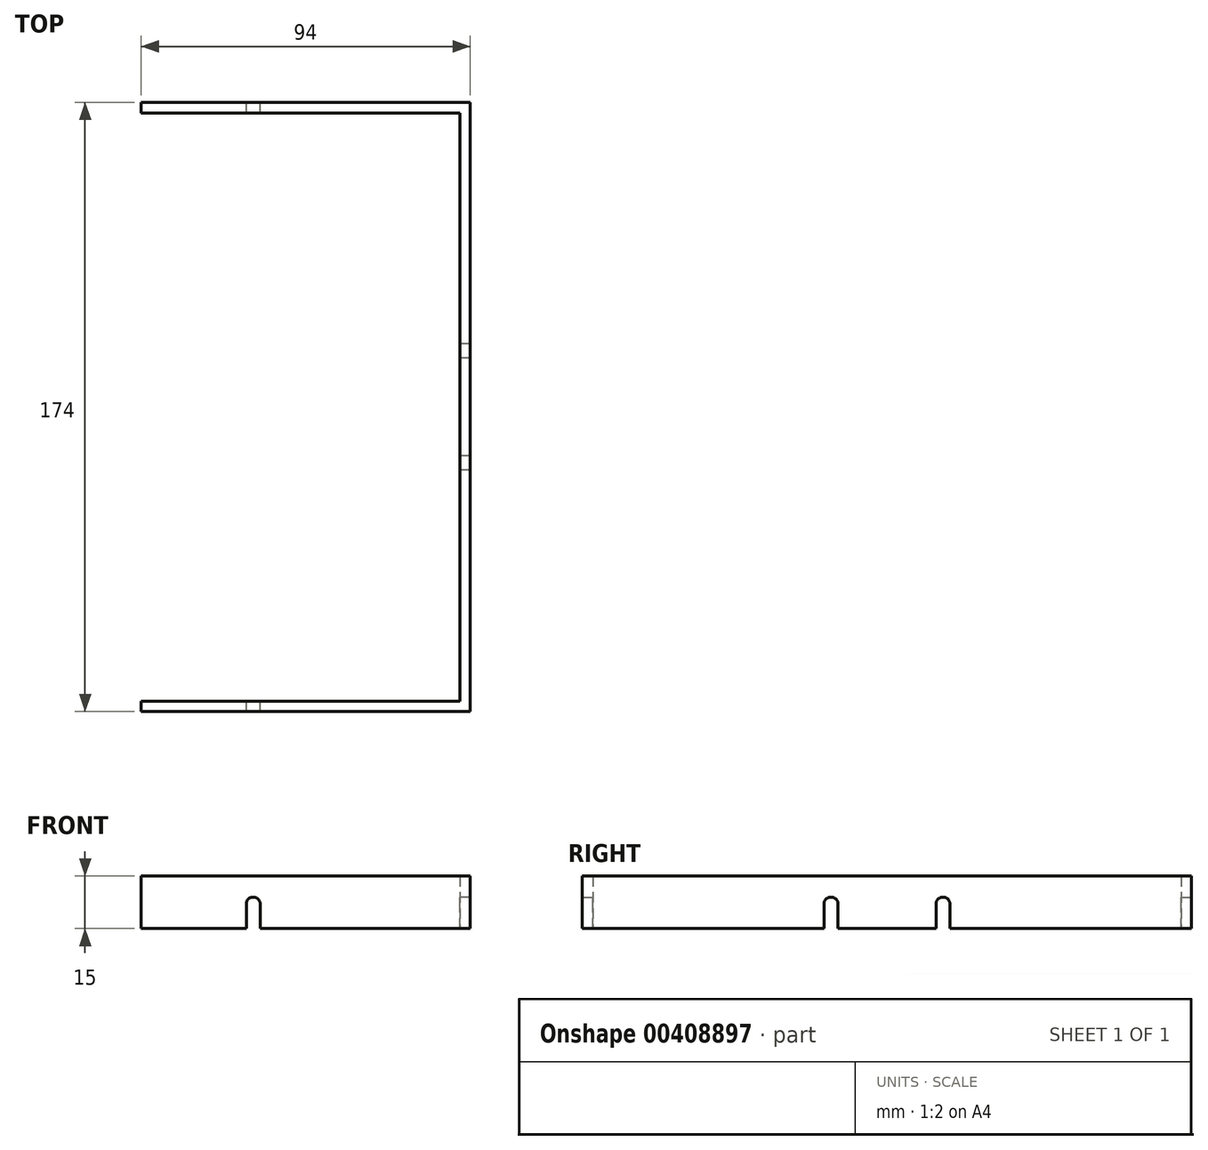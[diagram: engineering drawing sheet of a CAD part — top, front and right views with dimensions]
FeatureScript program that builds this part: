
annotation { "Feature Type Name" : "Feature", "Feature Type Description" : "" }
export const myFeature = defineFeature(function(context is Context, id is Id, definition is map)
    precondition{}
    {
        {
            var Q0;
            Q0=qCreatedBy(makeId("Top.planeOp"),FACE);
            var sketch = newSketch(context, id + "F0", { "sketchPlane" : qUnion([Q0])});
            skLineSegment(sketch, "E0.bottom", {"start": v(47, 87) * mm, "end": v(-47, 87) * mm});
            skLineSegment(sketch, "E0.top", {"start": v(47, -87) * mm, "end": v(-47, -87) * mm});
            skLineSegment(sketch, "E0.left", {"start": v(47, 87) * mm, "end": v(47, -87) * mm});
            skLineSegment(sketch, "E0.right", {"start": v(-47, 87) * mm, "end": v(-47, -87) * mm});
            skPoint(sketch, "E0.middle", {"position": v(0, 0) * mm});
            skSolve(sketch);
        }
        {
            var Q0;
            Q0=makeQuery(id+"F0.imprint","IMPRINT",FACE,{"disambiguationData":[TD([[makeQuery(id+"F0.imprint","IMPRINT",EDGE,{"derivedFrom":sQuery(id+"F0.wireOp",EDGE,"E0.bottom")}),1.0]])]});
            extrude(context, id + "F1", {"entities" : qUnion([Q0]), "depth" : 15 * mm});
        }
        {
            var Q0;
            Q0=makeQuery(id+"F1.opExtrude","CAP_FACE",FACE,{"disambiguationData":[OSD([sQuery(id+"F0.wireOp",EDGE,"E0.bottom"),sQuery(id+"F0.wireOp",EDGE,"E0.top"),sQuery(id+"F0.wireOp",EDGE,"E0.left"),sQuery(id+"F0.wireOp",EDGE,"E0.right")])],"isStart":false});
            var Q1;
            Q1=makeQuery(id+"F1.opExtrude","SWEPT_FACE",FACE,{"disambiguationData":[OSD([sQuery(id+"F0.wireOp",EDGE,"E0.right")])]});
            var Q2;
            Q2=makeQuery(id+"F1.opExtrude","CAP_FACE",FACE,{"disambiguationData":[OSD([sQuery(id+"F0.wireOp",EDGE,"E0.bottom"),sQuery(id+"F0.wireOp",EDGE,"E0.top"),sQuery(id+"F0.wireOp",EDGE,"E0.left"),sQuery(id+"F0.wireOp",EDGE,"E0.right")])],"isStart":true});
            shell(context, id + "F2", {"entities" : qUnion([Q0, Q1, Q2]), "thickness" : 3 * mm});
        }
        {
            var Q0;
            Q0=qCreatedBy(makeId("Right.planeOp"),FACE);
            var sketch = newSketch(context, id + "F3", { "sketchPlane" : qUnion([Q0])});
            skCircle(sketch, "E1", {"center": v(-16, 7) * mm, "radius": 2 * mm});
            skCircle(sketch, "E2.1.0.0", {"center": v(16, 7) * mm, "radius": 2 * mm});
            skLineSegment(sketch, "E2.direction1", {"start": v(-16, 7) * mm, "end": v(16, 7) * mm, "construction": true});
            skLineSegment(sketch, "E3.bottom", {"start": v(-18, 7) * mm, "end": v(-14, 7) * mm});
            skLineSegment(sketch, "E3.top", {"start": v(-18, 0) * mm, "end": v(-14, 0) * mm});
            skLineSegment(sketch, "E3.left", {"start": v(-18, 7) * mm, "end": v(-18, 0) * mm});
            skLineSegment(sketch, "E3.right", {"start": v(-14, 7) * mm, "end": v(-14, 0) * mm});
            skLineSegment(sketch, "E4.direction1", {"start": v(-14, 0) * mm, "end": v(18, 0) * mm, "construction": true});
            skLineSegment(sketch, "E5.1.0.0", {"start": v(18, 7) * mm, "end": v(18, 0) * mm});
            skLineSegment(sketch, "E5.1.0.1", {"start": v(14, 7) * mm, "end": v(18, 7) * mm});
            skLineSegment(sketch, "E5.1.0.2", {"start": v(14, 7) * mm, "end": v(14, 0) * mm});
            skLineSegment(sketch, "E5.1.0.3", {"start": v(14, 0) * mm, "end": v(18, 0) * mm});
            skLineSegment(sketch, "E5.direction1", {"start": v(-18, 0) * mm, "end": v(14, 0) * mm, "construction": true});
            skSolve(sketch);
        }
        {
            var Q0;
            Q0 = qSketchRegion(id + "F3", true);
            extrude(context, id + "F4", {"entities" : qUnion([Q0]), "operationType" : NewBodyOperationType.REMOVE, "oppositeDirection" : true, "depth" : -100 * mm});
        }
        {
            var Q0;
            Q0=qCreatedBy(makeId("Front.planeOp"),FACE);
            var sketch = newSketch(context, id + "F5", { "sketchPlane" : qUnion([Q0])});
            skCircle(sketch, "E6", {"center": v(-15, 7) * mm, "radius": 2 * mm});
            skLineSegment(sketch, "E7.bottom", {"start": v(-17, 7) * mm, "end": v(-13, 7) * mm});
            skLineSegment(sketch, "E7.top", {"start": v(-17, 0) * mm, "end": v(-13, 0) * mm});
            skLineSegment(sketch, "E7.left", {"start": v(-17, 7) * mm, "end": v(-17, 0) * mm});
            skLineSegment(sketch, "E7.right", {"start": v(-13, 7) * mm, "end": v(-13, 0) * mm});
            skSolve(sketch);
        }
        {
            var Q0;
            Q0 = qSketchRegion(id + "F5", true);
            extrude(context, id + "F6", {"entities" : qUnion([Q0]), "operationType" : NewBodyOperationType.REMOVE, "depth" : 250 * mm, "symmetric" : true});
        }
    });
